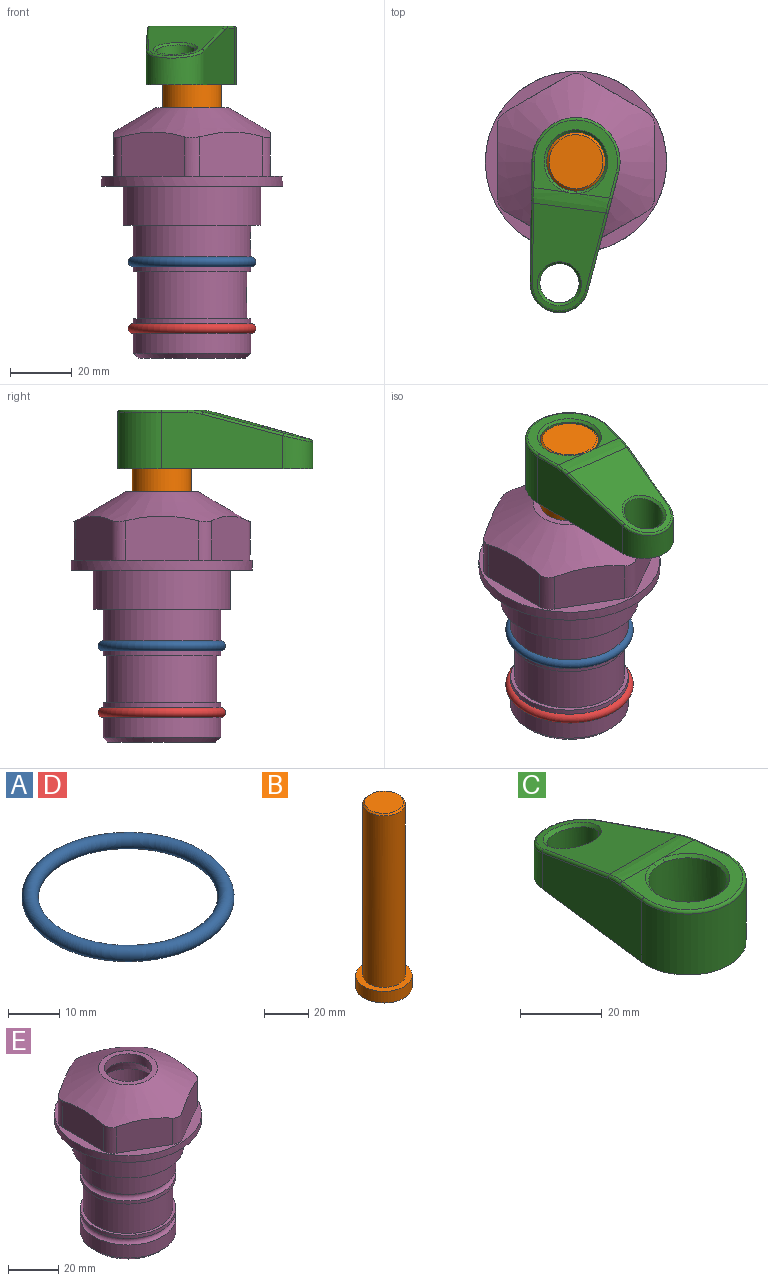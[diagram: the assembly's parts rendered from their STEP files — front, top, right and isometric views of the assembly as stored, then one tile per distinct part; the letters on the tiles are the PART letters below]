
ASSEMBLY  parts=5 mates=4
PART A: 1 faces, bbox 44.7x44.7x3.2 mm
  f0: torus R=19.05mm, axis (0,0,1), area 1193.9mm2
PART B: 6 faces, bbox 25.4x25.4x101.6 mm
  f0: plane 17.46x17.46mm, normal (0,0,1), area 239.5mm2, adj f5
  f1: plane 25.4x25.4mm, normal (0,0,-1), area 506.7mm2, adj f2
  f2: cylinder r=12.7mm len=25.4mm, axis (0,0,1), area 506.7mm2, adj f1,f3
  f3: plane 25.4x25.4mm, normal (0,0,1), area 221.7mm2, adj f2,f4
  f4: cylinder r=9.53mm len=94.46mm, axis (0,0,1), area 5653mm2, adj f3,f5
  f5: cone r=8.73mm half-angle=45deg, axis (0,0,-1), area 64.4mm2, adj f0,f4
PART C: 31 faces, bbox 31.7x65.5x19.8 mm
  f0: plane 39.12x18.26mm, normal (0.99,0.12,0), area 612.2mm2, adj f1,f4,f7,f11,f13,f15
  f1: cylinder r=9.53mm len=18.91mm, axis (0,0,-1), area 296.1mm2, adj f0,f2,f7,f17
  f2: plane 39.12x18.26mm, normal (-0.99,0.12,0), area 612.2mm2, adj f1,f4,f7,f12,f14,f16
  f3: cylinder r=6.35mm len=12.7mm, axis (0,0,-1), area 362.4mm2, adj f7,f18
  f4: cylinder r=14.29mm len=28.58mm, axis (0,0,-1), area 882.2mm2, adj f0,f2,f7,f10
  f5: cylinder r=9.53mm len=19.05mm, axis (0,0,-1), area 1092.6mm2, adj f7,f19,f20
  f6: plane 26.99x23.69mm, normal (0,0,1), area 216.2mm2, adj f9,f10,f11,f12,f19
  f7: plane 63.5x28.58mm, normal (0,0,-1), area 661.8mm2, adj f0,f1,f2,f3,f4,f5,f22,f23
  f8: plane 33.52x23.6mm, normal (0,0.26,0.97), area 486mm2, adj f9,f15,f16,f17,f18
  f9: cylinder r=19.05mm len=24.72mm, axis (1,0,0), area 120.4mm2, adj f6,f8,f13,f14,f20
  f10: torus R=13.49mm, axis (0,0,1), area 59mm2, adj f4,f6,f11,f12
  f11: cylinder r=0.79mm len=8.67mm, axis (0.12,-0.99,0), area 10.8mm2, adj f0,f6,f10,f13
  f12: cylinder r=0.79mm len=8.67mm, axis (0.12,0.99,0), area 10.8mm2, adj f2,f6,f10,f14
  f13: bspline ~4.95x1.42mm, area 6.1mm2, adj f0,f9,f11,f15
  f14: bspline ~4.95x1.42mm, area 6.1mm2, adj f2,f9,f12,f16
  f15: cylinder r=0.79mm len=25.95mm, axis (0.12,-0.96,0.26), area 32.9mm2, adj f0,f8,f13,f17
  f16: cylinder r=0.79mm len=25.95mm, axis (0.12,0.96,-0.26), area 32.9mm2, adj f2,f8,f14,f17
  f17: bspline ~18.91x8.38mm, area 30mm2, adj f1,f8,f15,f16
  f18: bspline ~14.29x14.29mm, area 48.3mm2, adj f3,f8
  f19: cone r=9.53mm half-angle=45deg, axis (0,0,1), area 66.5mm2, adj f5,f6,f20
  f20: bspline ~3.22x0.96mm, area 3.5mm2, adj f5,f9,f19
  f21: plane 2.75x2.72mm, normal (0,0,-1), area 2.9mm2, adj f23,f25,f28
  f22: plane 23.05x15.88mm, normal (-0.99,-0.12,0), area 323.6mm2, adj f7,f25,f26,f27,f28,f29
  f23: plane 23.05x15.88mm, normal (0.99,-0.12,0), area 323.6mm2, adj f7,f21,f25,f27,f28,f30
  f24: cylinder r=9.53mm len=10.69mm, axis (0,0,-1), area 114.7mm2, adj f7,f27,f29,f30
  f25: cylinder r=12.7mm len=20.59mm, axis (0,0,-1), area 381.1mm2, adj f7,f21,f22,f23,f26,f28
  f26: plane 2.75x2.72mm, normal (0,0,-1), area 2.9mm2, adj f22,f25,f28
  f27: plane 19.72x18.37mm, normal (0,-0.26,-0.97), area 291.8mm2, adj f22,f23,f24,f28,f29,f30
  f28: cylinder r=15.88mm len=19.92mm, axis (1,0,0), area 54.8mm2, adj f21,f22,f23,f25,f26,f27
  f29: cylinder r=1.59mm len=11mm, axis (0,0,-1), area 34.7mm2, adj f7,f22,f24,f27
  f30: cylinder r=1.59mm len=11mm, axis (0,0,-1), area 34.7mm2, adj f7,f23,f24,f27
PART D: same geometry as A
PART E: 36 faces, bbox 58.7x58.7x81 mm
  f0: cylinder r=17.78mm len=35.56mm, axis (0,0,1), area 1670.8mm2, adj f23,f24,f31
  f1: cylinder r=19.05mm len=38.1mm, axis (0,0,1), area 1191.9mm2, adj f26,f27,f30
  f2: plane 58.66x58.66mm, normal (0,0,-1), area 1150.6mm2, adj f3,f28
  f3: cylinder r=29.33mm len=58.66mm, axis (0,0,-1), area 585.1mm2, adj f2,f4
  f4: plane 58.66x58.66mm, normal (0,0,1), area 475.9mm2, adj f3,f5,f6,f7,f8,f9,f10,f11
  f5: plane 20.32x14.34mm, normal (-0.5,0.87,0), area 324.4mm2, adj f4,f15,f16,f17
  f6: plane 20.32x14.34mm, normal (0.5,0.87,0), area 324.4mm2, adj f4,f14,f15,f17
  f7: plane 23.48x14.34mm, normal (1,0,0), area 324.4mm2, adj f4,f13,f14,f17
  f8: plane 20.32x14.34mm, normal (0.5,-0.87,0), area 324.4mm2, adj f4,f12,f13,f17
  f9: plane 20.32x14.34mm, normal (-0.5,-0.87,0), area 324.4mm2, adj f4,f11,f12,f17
  f10: plane 23.48x14.34mm, normal (-1,0,0), area 324.4mm2, adj f4,f11,f16,f17
  f11: cylinder r=5.08mm len=12.85mm, axis (0,0,-1), area 67.2mm2, adj f4,f9,f10,f17
  f12: cylinder r=5.08mm len=12.85mm, axis (0,0,-1), area 67.2mm2, adj f4,f8,f9,f17
  f13: cylinder r=5.08mm len=12.85mm, axis (0,0,-1), area 67.2mm2, adj f4,f7,f8,f17
  f14: cylinder r=5.08mm len=12.85mm, axis (0,0,-1), area 67.2mm2, adj f4,f6,f7,f17
  f15: cylinder r=5.08mm len=12.85mm, axis (0,0,-1), area 67.2mm2, adj f4,f5,f6,f17
  f16: cylinder r=5.08mm len=12.85mm, axis (0,0,-1), area 67.2mm2, adj f4,f5,f10,f17
  f17: cone r=11.73mm half-angle=60deg, axis (0,0,-1), area 2071.8mm2, adj f5,f6,f7,f8,f9,f10,f11,f12
  f18: plane 23.46x23.46mm, normal (0,0,1), area 147.4mm2, adj f17,f35
  f19: plane 34.93x34.93mm, normal (0,0,-1), area 958mm2, adj f29
  f20: cylinder r=19.05mm len=38.1mm, axis (0,0,1), area 760.1mm2, adj f21,f29
  f21: torus R=19.05mm, axis (0,0,1), area 565.3mm2, adj f20,f22
  f22: cylinder r=19.05mm len=38.1mm, axis (0,0,1), area 190mm2, adj f21,f23
  f23: plane 38.1x38.1mm, normal (0,0,1), area 146.9mm2, adj f0,f22
  f24: plane 38.1x38.1mm, normal (0,0,-1), area 146.9mm2, adj f0,f25
  f25: cylinder r=19.05mm len=38.1mm, axis (0,0,1), area 190mm2, adj f24,f26
  f26: torus R=19.05mm, axis (0,0,1), area 565.3mm2, adj f1,f25
  f27: plane 44.45x44.45mm, normal (0,0,-1), area 411.7mm2, adj f1,f28
  f28: cylinder r=22.23mm len=44.45mm, axis (0,0,1), area 1773.5mm2, adj f2,f27
  f29: cone r=19.05mm half-angle=45deg, axis (0,0,1), area 257.5mm2, adj f19,f20
  f30: cylinder r=3.17mm len=6.75mm, axis (-1,0,0), area 128mm2, adj f1,f33
  f31: cylinder r=3.17mm len=6.35mm, axis (-1,0,0), area 102.5mm2, adj f0,f33
  f32: plane 25.4x25.4mm, normal (0,0,1), area 506.7mm2, adj f33
  f33: cylinder r=12.7mm len=66.42mm, axis (0,0,-1), area 5236.2mm2, adj f30,f31,f32,f34
  f34: cone r=9.53mm half-angle=30deg, axis (0,0,-1), area 443.4mm2, adj f33,f35
  f35: cylinder r=9.53mm len=19.05mm, axis (0,0,-1), area 240.9mm2, adj f18,f34
PLACE A at identity
PLACE B rot(axis=(0,0,1),172.3deg) t=(0,0,-12.45)mm
PLACE C rot(axis=(0,0,1),172.3deg) t=(0,0,-11.65)mm
PLACE D t=(0,0,-21.59)mm
PLACE E at identity fixed
MATE cylindrical B.f2 <-> E.f0  axis (0,0,-1) through (0,0,-50.55)mm
MATE fastened D.f0 <-> E.f0  axis (0,0,1) through (0,0,-46.1)mm
MATE fastened B.f2 <-> C.f4  axis (0,0,1) through (0,0,51.05)mm
MATE fastened A.f0 <-> E.f0  axis (0,0,1) through (0,0,-24.51)mm
